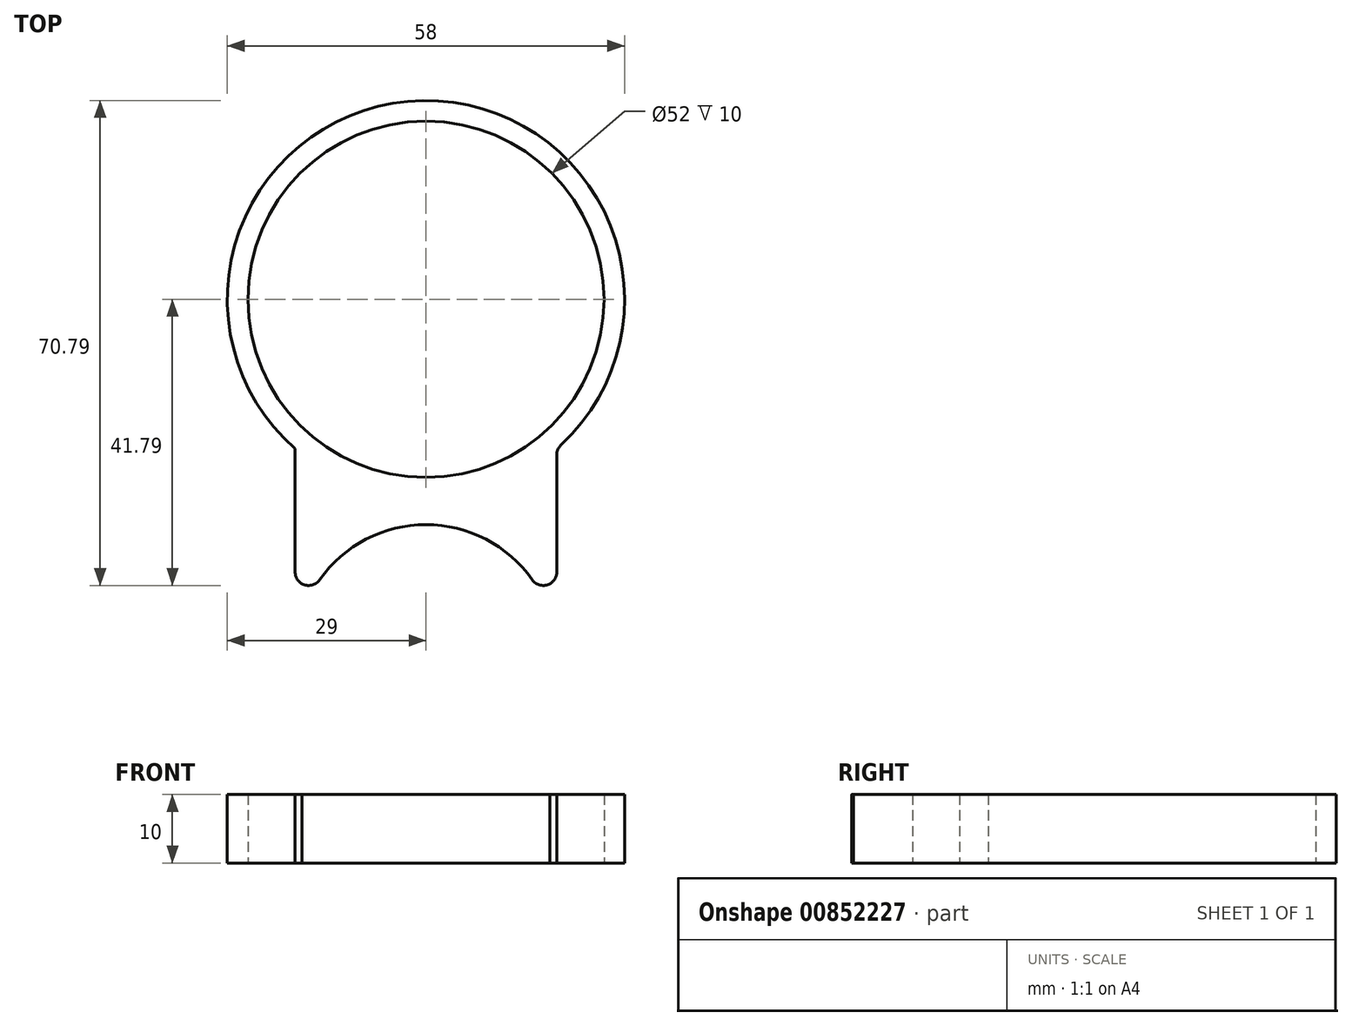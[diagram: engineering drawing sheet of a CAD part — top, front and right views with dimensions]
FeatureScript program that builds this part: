
annotation { "Feature Type Name" : "Feature", "Feature Type Description" : "" }
export const myFeature = defineFeature(function(context is Context, id is Id, definition is map)
    precondition{}
    {
        {
            var Q0;
            Q0=qCreatedBy(makeId("Top.planeOp"),FACE);
            var sketch = newSketch(context, id + "F0", { "sketchPlane" : qUnion([Q0])});
            skCircle(sketch, "E0", {"center": v(0, 0) * mm, "radius": 26 * mm});
            skCircle(sketch, "E1", {"center": v(0, 0) * mm, "radius": 29 * mm});
            skLineSegment(sketch, "E2", {"start": v(0, 0) * mm, "end": v(0, -75.45) * mm, "construction": true});
            skCircle(sketch, "E3", {"center": v(0, -52) * mm, "radius": 19.05 * mm, "construction": true});
            skCircle(sketch, "E4", {"center": v(0, -52) * mm, "radius": 22.05 * mm, "construction": true});
            skLineSegment(sketch, "E5", {"start": v(0, -52) * mm, "end": v(-34.24, -32.23) * mm, "construction": true});
            skLineSegment(sketch, "E6.MirrorCS", {"start": v(0, -52) * mm, "end": v(34.24, -32.23) * mm, "construction": true});
            skArc(sketch, "E7", {"start": v(19.1, -40.97) * mm, "mid": v(0, -29.9) * mm, "end": v(-19.1, -40.97) * mm});
            skArc(sketch, "E8", {"start": v(16.5, -42.48) * mm, "mid": v(0, -32.9) * mm, "end": v(-16.5, -42.48) * mm});
            skLineSegment(sketch, "E9", {"start": v(-16.5, -42.48) * mm, "end": v(-19.1, -40.98) * mm});
            skLineSegment(sketch, "E10", {"start": v(19.1, -40.97) * mm, "end": v(16.5, -42.48) * mm});
            skLineSegment(sketch, "E11", {"start": v(-19.1, -40.97) * mm, "end": v(-19.1, -21.83) * mm});
            skLineSegment(sketch, "E12.MirrorCS", {"start": v(19.1, -40.97) * mm, "end": v(19.1, -21.83) * mm});
            skSolve(sketch);
        }
        {
            var Q0;
            Q0 = qSketchRegion(id + "F0", true);
            extrude(context, id + "F1", {"entities" : qUnion([Q0]), "depth" : 10 * mm, "offsetDistance" : 25 * mm});
        }
        {
            var Q0;
            Q0=makeQuery(id+"F1.opExtrude","SWEPT_EDGE",EDGE,{"disambiguationData":[OSD([sQuery(id+"F0.wireOp",EDGE,"E7"),sQuery(id+"F0.wireOp",EDGE,"E9"),sQuery(id+"F0.wireOp",EDGE,"E11")])]});
            var Q1;
            Q1=makeQuery(id+"F1.opExtrude","SWEPT_EDGE",EDGE,{"disambiguationData":[OSD([sQuery(id+"F0.wireOp",EDGE,"E7"),sQuery(id+"F0.wireOp",EDGE,"E10"),sQuery(id+"F0.wireOp",EDGE,"E12.MirrorCS")])]});
            var Q2;
            Q2=makeQuery(id+"F1.opExtrude","SWEPT_EDGE",EDGE,{"disambiguationData":[OSD([sQuery(id+"F0.wireOp",EDGE,"E8"),sQuery(id+"F0.wireOp",EDGE,"E9")])]});
            var Q3;
            Q3=makeQuery(id+"F1.opExtrude","SWEPT_EDGE",EDGE,{"disambiguationData":[OSD([sQuery(id+"F0.wireOp",EDGE,"E8"),sQuery(id+"F0.wireOp",EDGE,"E10")])]});
            var Q4;
            Q4=makeQuery(id+"F1.opExtrude","SWEPT_EDGE",EDGE,{"disambiguationData":[OSD([sQuery(id+"F0.wireOp",EDGE,"E1"),sQuery(id+"F0.wireOp",EDGE,"E12.MirrorCS")])]});
            fillet(context, id + "F2", {"entities" : qUnion([Q0, Q1, Q2, Q3, Q4]), "radius" : 2 * mm, "tangentPropagation" : true, "allowEdgeOverflow" : false});
        }
    });
